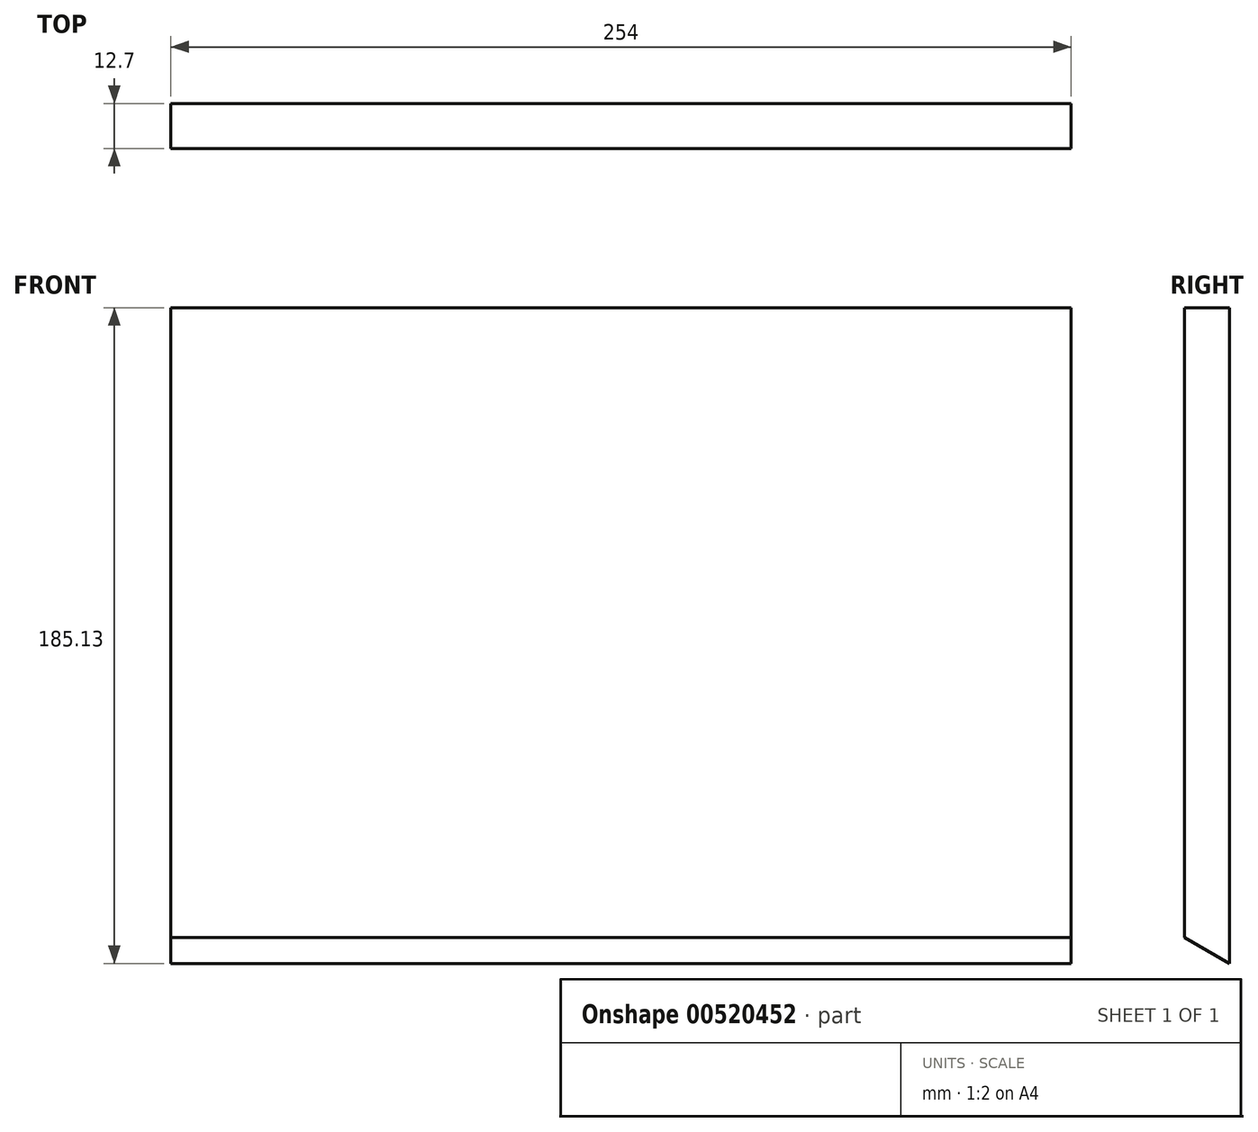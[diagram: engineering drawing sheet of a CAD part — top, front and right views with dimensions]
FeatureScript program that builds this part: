
annotation { "Feature Type Name" : "Feature", "Feature Type Description" : "" }
export const myFeature = defineFeature(function(context is Context, id is Id, definition is map)
    precondition{}
    {
        {
            var Q0;
            Q0=qCreatedBy(makeId("Front.planeOp"),FACE);
            var sketch = newSketch(context, id + "F0", { "sketchPlane" : qUnion([Q0])});
            skLineSegment(sketch, "E0.bottom", {"start": v(-123.63, 114.35) * mm, "end": v(130.37, 114.35) * mm});
            skLineSegment(sketch, "E0.top", {"start": v(-123.63, -76.15) * mm, "end": v(130.37, -76.15) * mm});
            skLineSegment(sketch, "E0.left", {"start": v(-123.63, 114.35) * mm, "end": v(-123.63, -76.15) * mm});
            skLineSegment(sketch, "E0.right", {"start": v(130.37, 114.35) * mm, "end": v(130.37, -76.15) * mm});
            skSolve(sketch);
        }
        {
            var Q0;
            Q0=makeQuery(id+"F0.imprint","IMPRINT",FACE,{"disambiguationData":[TD([[makeQuery(id+"F0.imprint","IMPRINT",EDGE,{"derivedFrom":sQuery(id+"F0.wireOp",EDGE,"E0.bottom")}),-1.0]])]});
            extrude(context, id + "F1", {"entities" : qUnion([Q0]), "depth" : 12.7 * mm, "offsetDistance" : 25.4 * mm});
        }
        {
            var Q0;
            Q0=makeQuery(id+"F1.opExtrude","CAP_EDGE",EDGE,{"disambiguationData":[OSD([sQuery(id+"F0.wireOp",EDGE,"E0.top")])],"isStart":false});
            chamfer(context, id + "F2", {"entities" : qUnion([Q0]), "chamferType" : ChamferType.OFFSET_ANGLE, "width" : 12.7 * mm, "oppositeDirection" : false, "angle" : 60 * degree, "tangentPropagation" : true});
        }
    });
